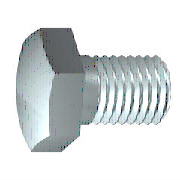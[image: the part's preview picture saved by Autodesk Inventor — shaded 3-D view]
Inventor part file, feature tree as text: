
AUTODESK INVENTOR PART (.ipt)
format: ipt  version: 2013 (Build 170138000, 138)  size: 186,368 bytes
history: native  units: mm (DEFAULTED — no unit token found)
features: sketch x2, extrude x1, chamfer x1, plane x1
ambient origin geometry x7: Origin, YZ Plane, XZ Plane, X Axis, Y Axis, Z Axis, Center Point
bodies: Solid1 (feature_tree), Body (feature_tree)
feature tree (5):
  extrude  "Head"  TaperAngle=90.0deg  [1 undecoded]
  chamfer  "Chamfer1"  [1 undecoded]
  plane  "Work Plane1"
  sketch  "Sketch1"  dims[d2=8.0mm d12=90.0deg]
  sketch  "Sketch2"  dims[d3=5.68mm d4=0.0mm d21=90.0deg d6=0.766813mm d7=0.766912mm d8=0.0mm d11=13.0mm d15=22.0mm d16=0.0mm d55=45.0deg d58=0.0mm d59=100.0mm d65=13.0mm d67=30.0deg d68=15.6mm d69=5.68mm d71=0.1mm d73=0.0mm]
note: 2 required parameter values undecoded (feature->parameter linkage not recoverable at this tier; creation-order binding heuristic only, values carry confidence <= 0.55)
